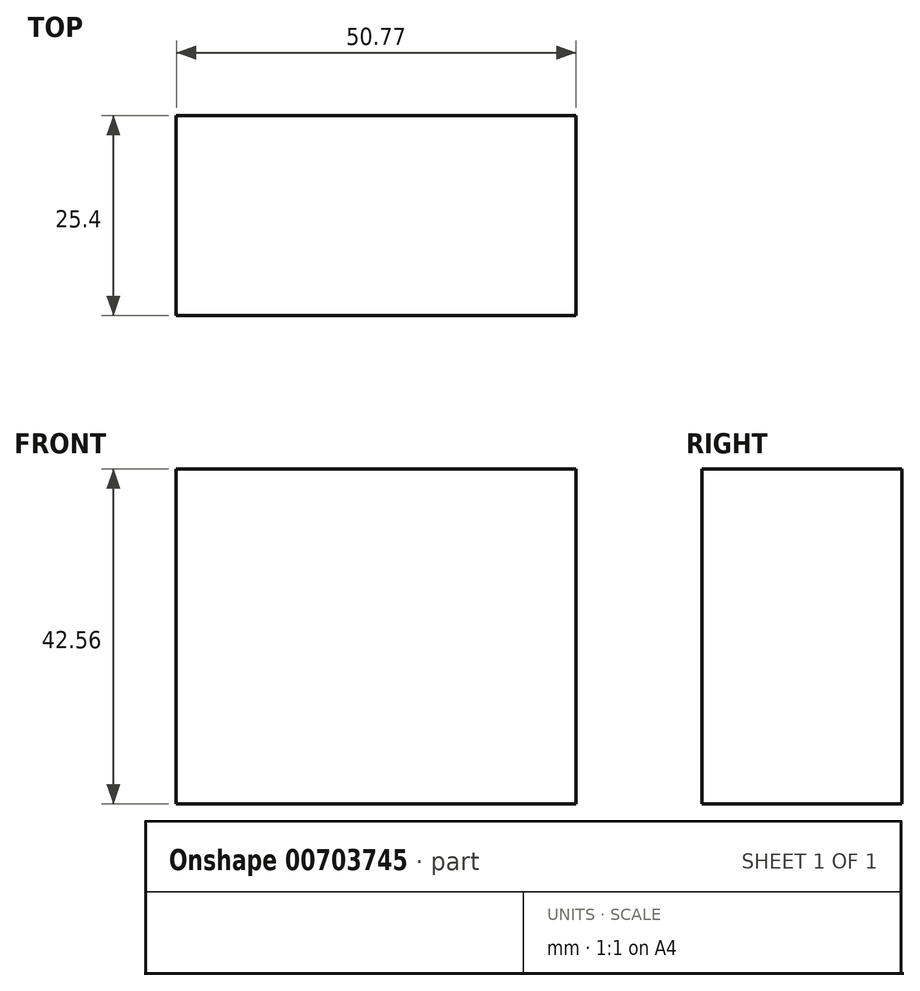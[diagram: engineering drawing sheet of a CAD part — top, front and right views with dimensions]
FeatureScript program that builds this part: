
annotation { "Feature Type Name" : "Feature", "Feature Type Description" : "" }
export const myFeature = defineFeature(function(context is Context, id is Id, definition is map)
    precondition{}
    {
        {
            var Q0;
            Q0=qCreatedBy(makeId("Front.planeOp"),FACE);
            var sketch = newSketch(context, id + "F0", { "sketchPlane" : qUnion([Q0])});
            skLineSegment(sketch, "E0.bottom", {"start": v(-14.31, -26.23) * mm, "end": v(36.46, -26.23) * mm});
            skLineSegment(sketch, "E0.top", {"start": v(-14.31, 16.33) * mm, "end": v(36.46, 16.33) * mm});
            skLineSegment(sketch, "E0.left", {"start": v(-14.31, -26.23) * mm, "end": v(-14.31, 16.33) * mm});
            skLineSegment(sketch, "E0.right", {"start": v(36.46, -26.23) * mm, "end": v(36.46, 16.33) * mm});
            skSolve(sketch);
        }
        {
            var Q0;
            Q0=makeQuery(id+"F0.imprint","IMPRINT",FACE,{"disambiguationData":[TD([[makeQuery(id+"F0.imprint","IMPRINT",EDGE,{"derivedFrom":sQuery(id+"F0.wireOp",EDGE,"E0.bottom")}),1.0]])]});
            extrude(context, id + "F1", {"entities" : qUnion([Q0]), "depth" : 25.4 * mm, "offsetDistance" : 25.4 * mm});
        }
    });
